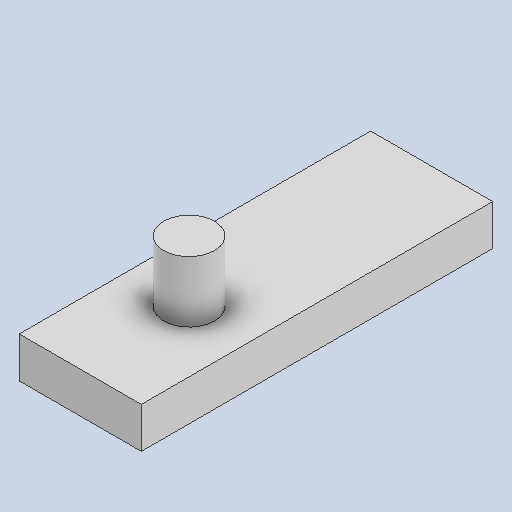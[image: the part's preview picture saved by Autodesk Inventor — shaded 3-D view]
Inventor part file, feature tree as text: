
AUTODESK INVENTOR PART (.ipt)
format: ipt  version: 2022 (Build 260153000, 153)  size: 103,424 bytes
history: native  units: in
note: dims shown in document units (in); Inventor stores cm internally (conversion verified against a paired STEP export)
features: extrude x2, sketch x2
ambient origin geometry x8: Origin, YZ Plane, XZ Plane, XY Plane, X Axis, Y Axis, Z Axis, Center Point
bodies: Body1 (feature_tree)
feature tree (4):
  extrude  "Extrusion6"  Depth=1.3602in
  extrude  "Extrusion7"  Depth=0.2362in
  sketch  "Sketch6"  dims[d22=0.4724in d23=1.3602in]
  sketch  "Sketch7"  dims[d24=0.1575in d25=0.0in d26=0.2362in d27=0.4213in d28=0.1969in d29=0.2362in d30=0.0in]
